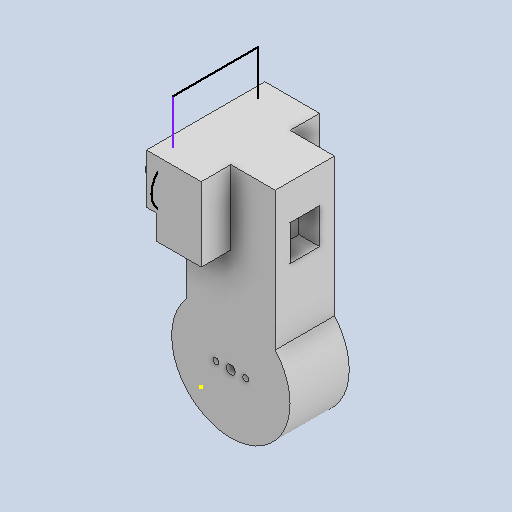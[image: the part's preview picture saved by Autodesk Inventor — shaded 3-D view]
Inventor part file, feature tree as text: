
AUTODESK INVENTOR PART (.ipt)
format: ipt  version: 2022 (Build 260153000, 153)  size: 327,168 bytes
history: native  units: in
note: dims shown in document units (in); Inventor stores cm internally (conversion verified against a paired STEP export)
features: sketch x28, extrude x22, chamfer x1
ambient origin geometry x8: Origin, YZ Plane, XZ Plane, XY Plane, X Axis, Y Axis, Z Axis, Center Point
bodies: Solid1 (feature_tree)
feature tree (51):
  extrude  "Extrusion1"  Depth=1.5748in
  extrude  "Extrusion2"  Depth=1.1811in
  extrude  "Extrusion3"  Depth=0.7874in
  extrude  "Extrusion4"  Depth=0.2362in
  extrude  "Extrusion5"  Depth=0.2362in
  extrude  "Extrusion6"  Depth=0.9055in TaperAngle=0.0deg
  extrude  "Extrusion7"  Depth=0.189in
  extrude  "Extrusion8"  Depth=0.6299in TaperAngle=0.0deg
  sketch  "Sketch11"  dims[d24=0.0984in d25=0.0591in]
  extrude  "Extrusion9"  Depth=0.0591in
  extrude  "Extrusion10"  Depth=0.0591in
  extrude  "Extrusion11"  Depth=0.3937in
  extrude  "Extrusion12"  Depth=0.1969in
  extrude  "Extrusion13"  Depth=0.1969in TaperAngle=0.0deg
  extrude  "Extrusion14"  Depth=0.0787in
  extrude  "Extrusion15"  Depth=0.1181in
  extrude  "Extrusion16"  Depth=0.3937in TaperAngle=0.0deg
  extrude  "Extrusion17"  Depth=0.3937in
  extrude  "Extrusion18"  Depth=0.3937in TaperAngle=0.0deg
  chamfer  "Chamfer2"  Distance=0.3937in
  sketch  "Sketch22"  dims[d56=0.9843in d57=0.3937in d58=0.0in]
  sketch  "Sketch25"  dims[d59=0.3937in d60=0.0in d61=0.9173in]
  sketch  "Sketch29"  dims[d62=0.7874in d63=0.3937in]
  extrude  "Extrusion24"  Depth=0.3937in TaperAngle=0.0deg
  extrude  "Extrusion27"  Depth=0.3937in
  sketch  "Sketch34"  dims[d67=0.1575in]
  extrude  "Extrusion28"  Depth=0.3937in
  extrude  "Extrusion29"  Depth=0.1575in
  sketch  "Sketch37"  dims[d72=0.7874in]
  sketch  "Sketch38"  dims[d73=0.6299in d74=0.0in d75=1.1826in d76=0.0in d77=0.0787in d78=0.0787in d79=5.4424in d80=0.0in d81=0.315in d82=0.0787in d83=45.0deg d92=0.6299in d93=0.6299in d94=0.6299in d99=0.9843in d104=0.315in d105=0.0in d110=0.3937in d111=0.315in d112=0.2756in d113=0.0in d114=0.1378in d115=0.0in d116=0.315in d117=0.0in]
  sketch  "Sketch1"  dims[d0=0.7874in d1=1.5748in]
  sketch  "Sketch2"  dims[d2=1.1811in d3=1.9685in]
  sketch  "Sketch4"  dims[d4=0.7874in d5=0.0in d6=0.7874in]
  sketch  "Sketch6"  dims[d7=0.5906in d8=0.0in d13=0.2362in]
  sketch  "Sketch7"  dims[d14=0.9843in d15=0.2362in]
  sketch  "Sketch8"  dims[d16=0.9055in d17=0.9055in d18=0.0in]
  sketch  "Sketch9"  dims[d19=0.4724in d20=0.189in]
  sketch  "Sketch10"  dims[d21=0.189in d22=0.6299in d23=0.0in]
  sketch  "Sketch12"  dims[d26=0.0984in d27=0.0591in]
  sketch  "Sketch13"  dims[d28=0.315in d29=0.0in d30=0.3937in]
  sketch  "Sketch15"  dims[d31=0.315in d32=0.1969in]
  sketch  "Sketch16"  dims[d33=0.1969in d34=0.6225in d35=0.0in]
  sketch  "Sketch17"  dims[d36=0.0787in d37=0.1181in]
  sketch  "Sketch18"  dims[d38=0.1181in d39=0.1181in]
  sketch  "Sketch19"  dims[d40=0.315in d41=0.0in d45=0.3937in d46=0.0in]
  sketch  "Sketch20"  dims[d47=0.5906in d48=0.3937in]
  sketch  "Sketch21"  dims[d49=2.3469in d50=0.0in d51=0.3937in d52=0.0in d53=0.3937in d54=0.0in]
  sketch  "Sketch30"  dims[d64=0.2362in d65=0.1575in]
  sketch  "Sketch33"  dims[d66=0.2362in]
  sketch  "Sketch35"  dims[d68=0.315in d69=0.0in]
  sketch  "Sketch36"  dims[d70=0.6299in d71=0.0in]
